# Revit family: Sink-Lab-Caroma Large1
name_source: partatom
category: Plumbing Fixtures
revit_build: Autodesk Revit Architecture 2012 (Build: 20110916_2132(x64)
units: mm (PartAtom-declared; Revit-internal decimal feet)

## types (1)
- Lab Sink Large
    Assembly Code = D2010430
    CW Connection = No
    Cost = 1018 $
    Default Elevation = 0 mm  [stored 0 ft]
    Depth_ANZRS = 265 mm  [stored 0.869423 ft]
    Description = Lab Sink Large
    HW Connection = No
    Keynote = SK
    Length_ANZRS = 405 mm  [stored 1.32874 ft]
    Manufacturer = Caroma
    Material_ANZRS = Porcelain-White-Caroma
    Model = 674103W
    ModifiedIssue_ANZRS = 1.1 $
    PlumbingMaterial_ANZRS = PVC-White-Caroma
    Type Comments = 50mm plug and waste not included
    URL = www.caroma.com.au
    Vent Connection = No
    WFU = 2
    Waste = Metal-Chrome-Caroma
    Waste Connection = Yes
    Waste Position = 135 mm  [stored 0.442913 ft]
    Width_ANZRS = 480 mm  [stored 1.5748 ft]

note: [stored X ft] marks values corroborated as IEEE doubles in the binary element streams (Revit-internal decimal feet)

## geometry (parser evidence)
native form markers: Blend x6, Sweep x1
no freeform markers — native parametric forms only
